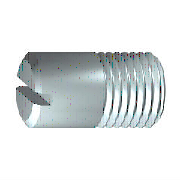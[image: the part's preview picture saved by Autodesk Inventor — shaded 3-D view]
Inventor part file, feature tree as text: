
AUTODESK INVENTOR PART (.ipt)
format: ipt  version: 2024 (Build 280153000, 153)  size: 160,768 bytes
history: native  units: mm (DEFAULTED — no unit token found)
features: other x2, extrude x1, plane x1
ambient origin geometry x8: Origin, YZ Plane, XZ Plane, XY Plane, X Axis, Y Axis, Z Axis, Center Point
bodies: Solid1 (feature_tree), Body (feature_tree)
feature tree (4):
  extrude  "Slot"  Depth=20.0mm
  other  "IDS_WORKPLANE"
  other  "Work Axis1"
  plane  "Work Plane2"
